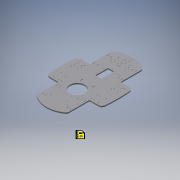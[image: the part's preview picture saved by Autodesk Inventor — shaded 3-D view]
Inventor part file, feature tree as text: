
AUTODESK INVENTOR PART (.ipt)
format: ipt  version: 2018 (Build 220112000, 112)  size: 678,400 bytes
history: native  units: in
note: dims shown in document units (in); Inventor stores cm internally (conversion verified against a paired STEP export)
features: extrude x16, sketch x14, other x5, fillet x4, reference x4
ambient origin geometry x8: Origin, YZ Plane, XZ Plane, XY Plane, X Axis, Y Axis, Z Axis, Center Point
bodies: Body1 (feature_tree)
feature tree (43):
  extrude  "Extrusion2"  Depth=0.25in
  sketch  "Sketch2"  dims[d4=0.25in d5=0.0in d24=0.5in]
  sketch  "Sketch3"  dims[d25=1.0in d103=9.36in]
  extrude  "Extrusion17"  Depth=9.36in
  extrude  "Extrusion21"  Depth=7.0in
  extrude  "Extrusion22"  Depth=0.3937in
  fillet  "Fillet1"  Radius=0.3937in
  extrude  "Extrusion28"  Depth=1.2in
  extrude  "Extrusion29"  Depth=0.3937in
  extrude  "Extrusion30"  Depth=0.3937in
  extrude  "Extrusion31"  Depth=1.2752in
  extrude  "Extrusion32"  Depth=0.1378in
  fillet  "Fillet2"  Radius=0.1378in
  fillet  "Fillet3"  Radius=0.1378in
  extrude  "Extrusion33"  Depth=0.3937in
  extrude  "Extrusion34"  Depth=0.1378in
  extrude  "Extrusion35"  Depth=0.3937in TaperAngle=0.0deg
  extrude  "Extrusion36"  Depth=0.1378in
  extrude  "Extrusion37"  Depth=0.0787in
  extrude  "Extrusion38"  Depth=0.0787in
  extrude  "Extrusion39"  Depth=0.3937in TaperAngle=0.0deg
  fillet  "Fillet4"  Radius=0.1378in
  reference  "Reference1"
  reference  "Reference2"
  reference  "Reference3"
  reference  "Reference4"
  sketch  "Sketch16"  dims[d104=18.72in d105=7.0in]
  sketch  "Sketch22"  dims[d106=14.0in d107=3.0in d108=0.3937in d109=0.0in]
  sketch  "Sketch24"  dims[d110=0.1in d111=1.2in]
  sketch  "Sketch25"  dims[d123=0.3937in d124=0.0in d125=3.937in]
  sketch  "Sketch26"  dims[d126=0.3937in d127=0.0in d128=5.0in]
  sketch  "Sketch29"  dims[d149=2.5504in d150=1.2752in]
  sketch  "Sketch30"  dims[d172=0.1378in d173=0.1378in d174=0.1378in d175=0.1378in]
  sketch  "Sketch31"  dims[d176=0.3937in d177=0.0in d178=0.1378in]
  sketch  "Sketch32"  dims[d179=0.1378in d180=0.1378in]
  sketch  "Sketch33"  dims[d181=0.1378in d182=0.3937in d183=0.0in]
  sketch  "Sketch34"  dims[d186=0.1378in d187=0.1378in]
  sketch  "Sketch35"  dims[d188=0.1378in d189=0.1378in d190=0.1378in d191=0.3937in d192=0.0in d193=0.1378in d194=0.1378in d195=0.1378in d196=0.1378in d197=0.1378in d198=0.1378in d199=0.1378in d200=0.9843in d202=0.2756in d203=0.1378in d204=0.3937in d205=0.0in d206=0.1378in d207=0.1378in d208=0.1378in d209=0.1378in d210=0.1378in d211=0.1378in d212=0.1378in d213=0.1378in d214=0.1378in d215=0.315in d216=3.937in d217=0.1969in d218=5.9055in d219=0.3937in d220=0.0in d221=0.7874in d222=0.1969in d223=6.6929in d224=3.2677in d229=0.5197in d230=1.0394in d235=0.0787in d236=0.1575in d237=0.0787in d238=0.0787in d239=0.3937in d240=0.0in d241=0.6004in d242=0.6004in d243=0.1181in d244=0.1181in d245=0.6004in d246=0.1181in d247=0.3937in d248=0.0in d249=0.1969in d250=2.3985in d251=2.3985in d252=4.7514in d253=0.1969in d254=0.1181in d255=0.3937in d256=0.0in d257=0.1181in d258=0.1181in d259=0.1181in d260=0.1181in d261=0.3937in d262=0.0in d263=0.1181in d264=0.1181in d265=0.1181in d266=0.1181in d267=0.1181in d268=0.1181in d269=0.1181in d270=0.1181in d271=0.3937in d272=0.0in d273=0.1378in d274=0.1378in d275=0.1378in d276=0.1378in d277=0.1378in d278=0.1378in d279=0.1378in d280=0.1378in d281=0.1378in d282=0.1378in d283=0.3937in d284=0.0in d285=0.1378in d286=0.3937in d287=0.0in d288=0.0787in]
  other  "<userpath>\OneDrive\Documents\Inventor\TSA\2018\Animatronics\Tortoise\AssemblyTURTLE.iam"
  other  "AssemblyTURTLE.iam"
  other  "wheelframe:1"
  other  "wheelframe2:1"
  other  "correct_wheel:1"
